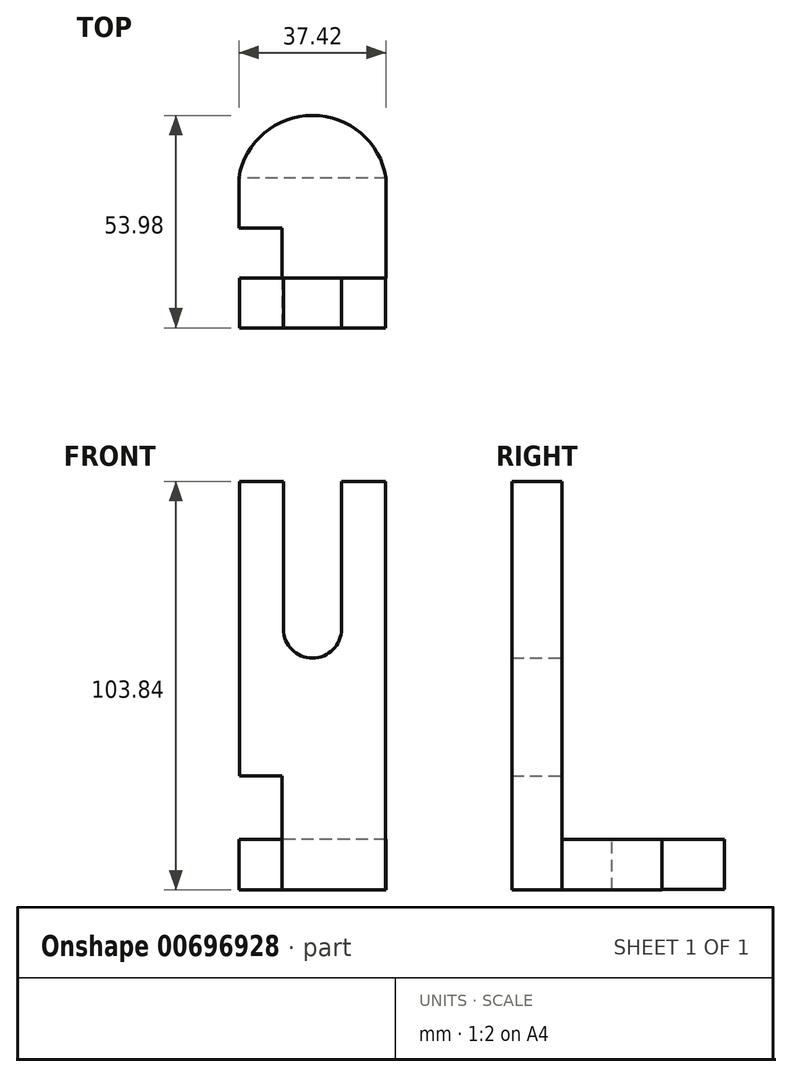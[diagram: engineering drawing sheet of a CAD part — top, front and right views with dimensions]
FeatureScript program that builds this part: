
annotation { "Feature Type Name" : "Feature", "Feature Type Description" : "" }
export const myFeature = defineFeature(function(context is Context, id is Id, definition is map)
    precondition{}
    {
        {
            var Q0;
            Q0=qCreatedBy(makeId("Front.planeOp"),FACE);
            var sketch = newSketch(context, id + "F0", { "sketchPlane" : qUnion([Q0])});
            skLineSegment(sketch, "E0.bottom", {"start": v(-18.6, 51.92) * mm, "end": v(-7.38, 51.92) * mm});
            skLineSegment(sketch, "E0.top", {"start": v(-18.6, -51.92) * mm, "end": v(18.6, -51.92) * mm});
            skLineSegment(sketch, "E0.left", {"start": v(-18.6, 51.92) * mm, "end": v(-18.6, -51.92) * mm});
            skLineSegment(sketch, "E0.right", {"start": v(18.6, 51.92) * mm, "end": v(18.6, -51.92) * mm});
            skPoint(sketch, "E0.middle", {"position": v(0, 0) * mm});
            skLineSegment(sketch, "E1.left", {"start": v(-7.38, 51.92) * mm, "end": v(-7.38, 14.4) * mm});
            skLineSegment(sketch, "E1.right", {"start": v(7.38, 51.92) * mm, "end": v(7.38, 14.4) * mm});
            skPoint(sketch, "E1.middle", {"position": v(0, 33.16) * mm});
            skArc(sketch, "E2", {"start": v(-7.38, 14.4) * mm, "mid": v(0, 7.02) * mm, "end": v(7.38, 14.4) * mm});
            skLineSegment(sketch, "E3.trimOffspring", {"start": v(7.38, 51.92) * mm, "end": v(18.6, 51.92) * mm});
            skSolve(sketch);
        }
        {
            var Q0;
            Q0 = qSketchRegion(id + "F0", true);
            extrude(context, id + "F1", {"entities" : qUnion([Q0]), "depth" : 12.7 * mm, "offsetDistance" : 25.4 * mm});
        }
        {
            var Q0;
            Q0=qCreatedBy(makeId("Front.planeOp"),FACE);
            var sketch = newSketch(context, id + "F2", { "sketchPlane" : qUnion([Q0])});
            skLineSegment(sketch, "E4.bottom", {"start": v(18.7, -38.98) * mm, "end": v(-18.7, -38.98) * mm});
            skLineSegment(sketch, "E4.top", {"start": v(18.7, -51.83) * mm, "end": v(-18.7, -51.83) * mm});
            skLineSegment(sketch, "E4.left", {"start": v(18.7, -38.98) * mm, "end": v(18.7, -51.83) * mm});
            skLineSegment(sketch, "E4.right", {"start": v(-18.7, -38.98) * mm, "end": v(-18.7, -51.83) * mm});
            skSolve(sketch);
        }
        {
            var Q0;
            Q0=makeQuery(id+"F2.imprint","IMPRINT",FACE,{"disambiguationData":[TD([[makeQuery(id+"F2.imprint","IMPRINT",EDGE,{"derivedFrom":sQuery(id+"F2.wireOp",EDGE,"E4.bottom")}),1.0]])]});
            extrude(context, id + "F3", {"entities" : qUnion([Q0]), "operationType" : NewBodyOperationType.ADD, "oppositeDirection" : true, "depth" : 25.4 * mm, "offsetDistance" : 25.4 * mm});
        }
        {
            var Q0;
            Q0=makeQuery(id+"F3.opExtrude","SWEPT_FACE",FACE,{"disambiguationData":[OSD([sQuery(id+"F2.wireOp",EDGE,"E4.bottom")])]});
            var sketch = newSketch(context, id + "F4", { "sketchPlane" : qUnion([Q0])});
            skArc(sketch, "E5", {"start": v(18.7, 25.4) * mm, "mid": v(0, 41.28) * mm, "end": v(-18.7, 25.4) * mm});
            skPoint(sketch, "E5.first.point", {"position": v(18.7, 25.4) * mm});
            skPoint(sketch, "E5.second.point", {"position": v(-18.7, 25.4) * mm});
            skPoint(sketch, "E5.third.point", {"position": v(-18.7, 19.26) * mm});
            skSolve(sketch);
        }
        {
            var Q0;
            Q0 = qSketchRegion(id + "F4", true);
            var Q1;
            Q1=makeQuery(id+"F4.imprint","IMPRINT",FACE,{"disambiguationData":[TD([[makeQuery(id+"F4.imprint","IMPRINT",EDGE,{"derivedFrom":sQuery(id+"F4.wireOp",EDGE,"E5")}),1.0]])]});
            extrude(context, id + "F5", {"entities" : qUnion([Q0, Q1]), "operationType" : NewBodyOperationType.ADD, "oppositeDirection" : true, "depth" : 12.7 * mm, "offsetDistance" : 25.4 * mm});
        }
        {
            var Q0;
            Q0=makeQuery(id+"F1.opExtrude","CAP_FACE",FACE,{"disambiguationData":[OSD([sQuery(id+"F0.wireOp",EDGE,"E0.bottom"),sQuery(id+"F0.wireOp",EDGE,"E0.top"),sQuery(id+"F0.wireOp",EDGE,"E0.left"),sQuery(id+"F0.wireOp",EDGE,"E0.right"),sQuery(id+"F0.wireOp",EDGE,"E1.left"),sQuery(id+"F0.wireOp",EDGE,"E1.right"),sQuery(id+"F0.wireOp",EDGE,"E2"),sQuery(id+"F0.wireOp",EDGE,"E3.trimOffspring")])],"isStart":false});
            var sketch = newSketch(context, id + "F6", { "sketchPlane" : qUnion([Q0])});
            skLineSegment(sketch, "E6.bottom", {"start": v(-32.07, -22.88) * mm, "end": v(-7.8, -22.88) * mm});
            skLineSegment(sketch, "E6.top", {"start": v(-32.07, -61.23) * mm, "end": v(-7.8, -61.23) * mm});
            skLineSegment(sketch, "E6.left", {"start": v(-32.07, -22.88) * mm, "end": v(-32.07, -61.23) * mm});
            skLineSegment(sketch, "E6.right", {"start": v(-7.8, -22.88) * mm, "end": v(-7.8, -61.23) * mm});
            skSolve(sketch);
        }
        {
            var Q0;
            Q0 = qSketchRegion(id + "F6", true);
            extrude(context, id + "F7", {"entities" : qUnion([Q0]), "operationType" : NewBodyOperationType.REMOVE, "oppositeDirection" : true, "depth" : 25.4 * mm, "offsetDistance" : 25.4 * mm});
        }
    });
